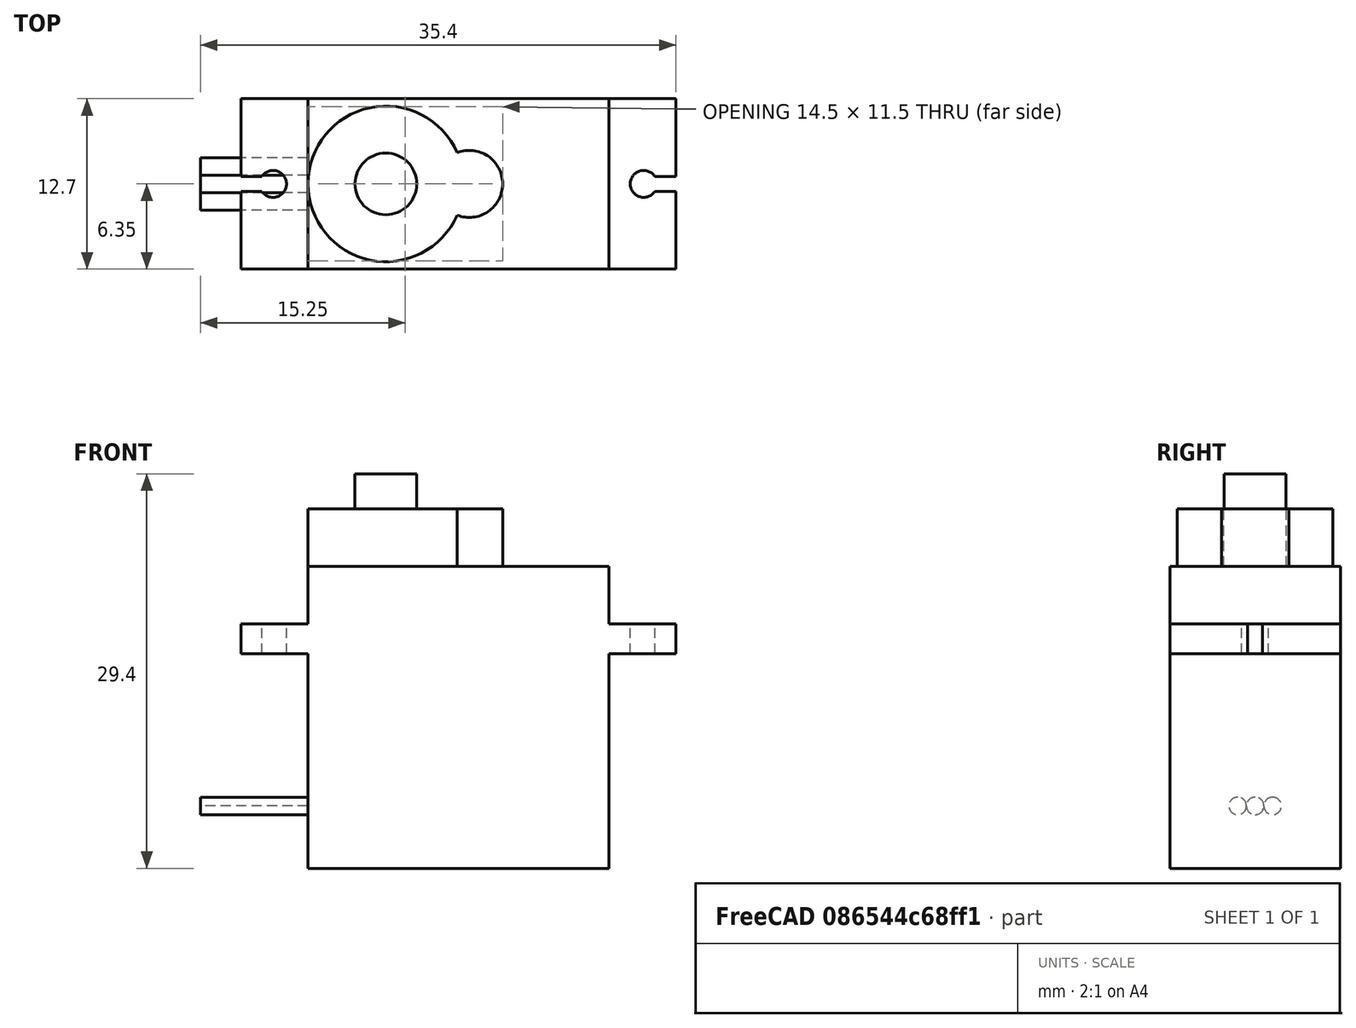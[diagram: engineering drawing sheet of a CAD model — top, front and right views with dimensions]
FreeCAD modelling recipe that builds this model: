
FCSTD DOCUMENT  (FreeCAD 0.17R12960 (Git))
Label: SG92R
License: All rights reserved
LicenseURL: http://en.wikipedia.org/wiki/All_rights_reserved
objects: Part::MultiFuse×8, Part::Cylinder×8, Part::Box×7, Part::Cut×4
note: 27 computed .brp shape members not serialized (recipe doc carries the construction recipe); baked Part::Feature solids carry a one-line shape summary decoded from their .brp

FEATURE [Part::Box] Box  label="Body"
  AttacherType = Attacher::AttachEngine3D
  Height = 22.5
  Length = 32.4
  Width = 12.7
FEATURE [Part::Box] Box001  label="LowerCutB"
  AttacherType = Attacher::AttachEngine3D
  Height = 16
  Length = 5
  Width = 12.7
FEATURE [Part::Box] Box002  label="LowerCutF"
  AttacherType = Attacher::AttachEngine3D
  Height = 16
  Length = 5
  Placement = pos=(27.4,0,0) rot=(0,0,1;0rad)
  Width = 12.7
FEATURE [Part::Cut] Cut
  Base = -> Box
  Tool = -> Box002
FEATURE [Part::Cut] Cut001  label="LowerBody"
  Base = -> Cut
  Tool = -> Box001
FEATURE [Part::Box] Box003  label="UpperCutB"
  AttacherType = Attacher::AttachEngine3D
  Height = 4.3
  Length = 5
  Width = 12.7
FEATURE [Part::Box] Box004  label="UpperCutF"
  AttacherType = Attacher::AttachEngine3D
  Height = 4.3
  Length = 5
  Placement = pos=(27.4,0,0) rot=(0,0,1;0rad)
  Width = 12.7
FEATURE [Part::MultiFuse] Fusion  label="UpperCuts"
  Placement = pos=(0,0,18.2) rot=(0,0,1;0rad)
  Shapes = -> [Box003,Box004]
FEATURE [Part::Cut] Cut002  label="BasicBody"
  Base = -> Cut001
  Tool = -> Fusion
FEATURE [Part::Cylinder] Cylinder  label="BigShaft"
  Angle = 360
  AttacherType = Attacher::AttachEngine3D
  Height = 26.8
  Placement = pos=(10.8,6.35,0) rot=(0,0,1;0rad)
  Radius = 5.8
FEATURE [Part::Cylinder] Cylinder001  label="Axis"
  Angle = 360
  AttacherType = Attacher::AttachEngine3D
  Height = 29.4
  Placement = pos=(10.8,6.35,0) rot=(0,0,1;0rad)
  Radius = 2.3
FEATURE [Part::Cylinder] Cylinder002  label="SideAxis"
  Angle = 360
  AttacherType = Attacher::AttachEngine3D
  Height = 26.8
  Placement = pos=(17,6.35,0) rot=(0,0,1;0rad)
  Radius = 2.5
FEATURE [Part::Cylinder] Cylinder003  label="CableR"
  Angle = 360
  AttacherType = Attacher::AttachEngine3D
  Height = 10
  Placement = pos=(0,0,0) rot=(0,-1,0;1.5708rad)
  Radius = 0.65
FEATURE [Part::Cylinder] Cylinder004  label="CableB"
  Angle = 360
  AttacherType = Attacher::AttachEngine3D
  Height = 10
  Placement = pos=(0,1.3,0) rot=(0,-1,0;1.5708rad)
  Radius = 0.65
FEATURE [Part::Cylinder] Cylinder005  label="CableY"
  Angle = 360
  AttacherType = Attacher::AttachEngine3D
  Height = 10
  Placement = pos=(0,-1.3,0) rot=(0,-1,0;1.5708rad)
  Radius = 0.65
FEATURE [Part::MultiFuse] Fusion003  label="Cables"
  Placement = pos=(7,6.35,4.65) rot=(0,0,1;0rad)
  Shapes = -> [Cylinder005,Cylinder003,Cylinder004]
FEATURE [Part::MultiFuse] Fusion004  label="InternalAxes"
  Shapes = -> [Cylinder,Cylinder002]
FEATURE [Part::MultiFuse] Fusion005  label="Axes"
  Shapes = -> [Fusion004,Cylinder001]
FEATURE [Part::Cylinder] Cylinder006  label="Zylinder"
  Angle = 360
  AttacherType = Attacher::AttachEngine3D
  Height = 10
  Radius = 1
FEATURE [Part::Box] Box005  label="Würfel"
  AttacherType = Attacher::AttachEngine3D
  Height = 10
  Length = 10
  Placement = pos=(-10,-0.55,0) rot=(0,0,1;0rad)
  Width = 1.1
FEATURE [Part::MultiFuse] Fusion007  label="DrillSlotB"
  Placement = pos=(2.4,0,0) rot=(0,0,1;0rad)
  Shapes = -> [Box005,Cylinder006]
FEATURE [Part::Cylinder] Cylinder007  label="Zylinder001"
  Angle = 360
  AttacherType = Attacher::AttachEngine3D
  Height = 10
  Radius = 1
FEATURE [Part::Box] Box006  label="Würfel001"
  AttacherType = Attacher::AttachEngine3D
  Height = 10
  Length = 10
  Placement = pos=(-10,-0.55,0) rot=(0,0,1;0rad)
  Width = 1.1
FEATURE [Part::MultiFuse] Fusion008  label="DrillSlotF"
  Placement = pos=(30,0,0) rot=(0,0,1;3.14159rad)
  Shapes = -> [Box006,Cylinder007]
FEATURE [Part::MultiFuse] Fusion009  label="DrillSlots"
  Placement = pos=(0,6.35,13) rot=(0,0,1;0rad)
  Shapes = -> [Fusion008,Fusion007]
FEATURE [Part::Cut] Cut003  label="CutBody"
  Base = -> Cut002
  Tool = -> Fusion009
FEATURE [Part::MultiFuse] Fusion010  label="SG92R"
  Shapes = -> [Fusion005,Fusion003,Cut003]
